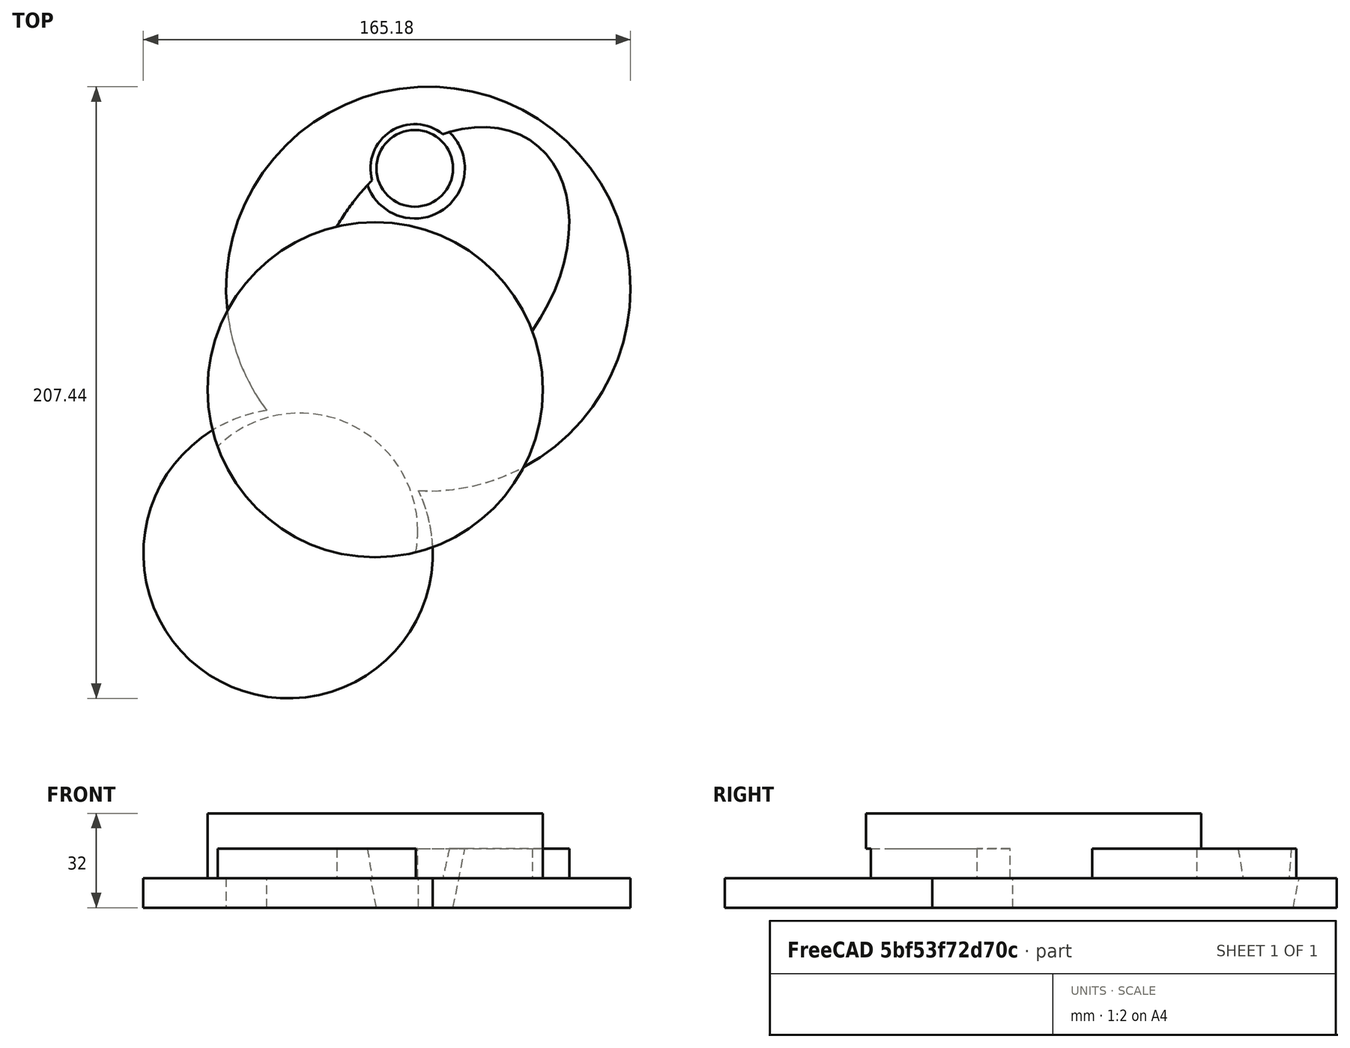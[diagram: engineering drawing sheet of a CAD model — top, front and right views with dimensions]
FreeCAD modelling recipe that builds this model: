
FCSTD DOCUMENT  (FreeCAD 0.17R13327 (Git))
Label: planing
License: All rights reserved
LicenseURL: http://en.wikipedia.org/wiki/All_rights_reserved
objects: Sketcher::SketchObject×3, PartDesign::Pad×3, Part::Cut×2, PartDesign::Body×1, Part::Cylinder×1, Part::Cone×1, Part::Feature×1
note: 15 computed .brp shape members not serialized (recipe doc carries the construction recipe); baked Part::Feature solids carry a one-line shape summary decoded from their .brp

FEATURE [Sketcher::SketchObject] Sketch
  MapMode = 5
  Support = -> [XY_Plane]
  sketch-geometry (2):
    g0: ArcOfCircle CenterX=-78.9463 CenterY=-20.6666 CenterZ=0 NormalX=0 NormalY=0 NormalZ=1 AngleXU=0 Radius=49.0864 StartAngle=1.71891 EndAngle=6.73216
    g1: ArcOfCircle CenterX=-31.4139 CenterY=69.1268 CenterZ=0 NormalX=0 NormalY=0 NormalZ=1 AngleXU=0 Radius=68.5676 StartAngle=4.66408 EndAngle=10.0702
  constraints (2):
    c: Coincident(g1,g0)
    c: Coincident(g1,g0)
FEATURE [PartDesign::Pad] Pad
  Length = 10
  Length2 = 100
  Profile = -> Sketch
  Type = 0
FEATURE [Sketcher::SketchObject] Sketch001
  MapMode = 5
  Placement = pos=(0,0,10) rot=(0,0,1;0rad)
  Support = -> [Pad]
  sketch-geometry (1):
    g0: Circle CenterX=-49.4159 CenterY=34.9349 CenterZ=0 NormalX=0 NormalY=0 NormalZ=1 AngleXU=0 Radius=56.8202
FEATURE [PartDesign::Pad] Pad001
  BaseFeature = -> Pad
  Length = 22
  Length2 = 100
  Profile = -> Sketch001
  Type = 0
FEATURE [Sketcher::SketchObject] Sketch002
  MapMode = 5
  Placement = pos=(0,0,10) rot=(0,0,1;0rad)
  Support = -> [Pad001]
  sketch-geometry (5):
    g0: Ellipse CenterX=-27.4261 CenterY=75.4969 CenterZ=0 NormalX=0 NormalY=0 NormalZ=1 MajorRadius=53.6075 MinorRadius=37.4058 AngleXU=-2.20728
    g1: LineSegment [constr] StartX=-59.2888 StartY=32.3863 StartZ=0 EndX=4.43664 EndY=118.608 EndZ=0
    g2: LineSegment [constr] StartX=2.65538 StartY=53.264 StartZ=0 EndX=-57.5075 EndY=97.7298 EndZ=0
    g3: GeomPoint [constr] X=-50.2499 Y=44.6159 Z=0
    g4: GeomPoint [constr] X=-4.60221 Y=106.378 Z=0
  constraints (1):
    c: InternalAlignment(g1-g4 -> g0) x4
FEATURE [PartDesign::Pad] Pad002
  BaseFeature = -> Pad001
  Length = 10
  Length2 = 100
  Profile = -> Sketch002
  Type = 0
FEATURE [PartDesign::Body] Body
  Group = -> [Sketch,Pad,Sketch001,Pad001,Sketch002,Pad002]
  Origin = -> BodyOrigin
  Tip = -> Pad002
FEATURE [Part::Cylinder] Cylinder
  Angle = 360
  AttacherType = Attacher::AttachEngine3D
  Height = 10
  Placement = pos=(-75,-13,10) rot=(0,0,1;0rad)
  Radius = 40
FEATURE [Part::Cut] Cut
  Base = -> Body
  Tool = -> Cylinder
FEATURE [Part::Cone] Cone
  Angle = 360
  AttacherType = Attacher::AttachEngine3D
  Height = 25
  Placement = pos=(-36,110,0) rot=(0,0,1;0rad)
  Radius1 = 13
  Radius2 = 18
FEATURE [Part::Cut] Cut001
  Base = -> Cut
  Tool = -> Cone
FEATURE [Part::Feature] Cut001001  label="Cut002"
  shape: bbox 165.2 x 207.4 x 32 mm, 15 faces (baked)
